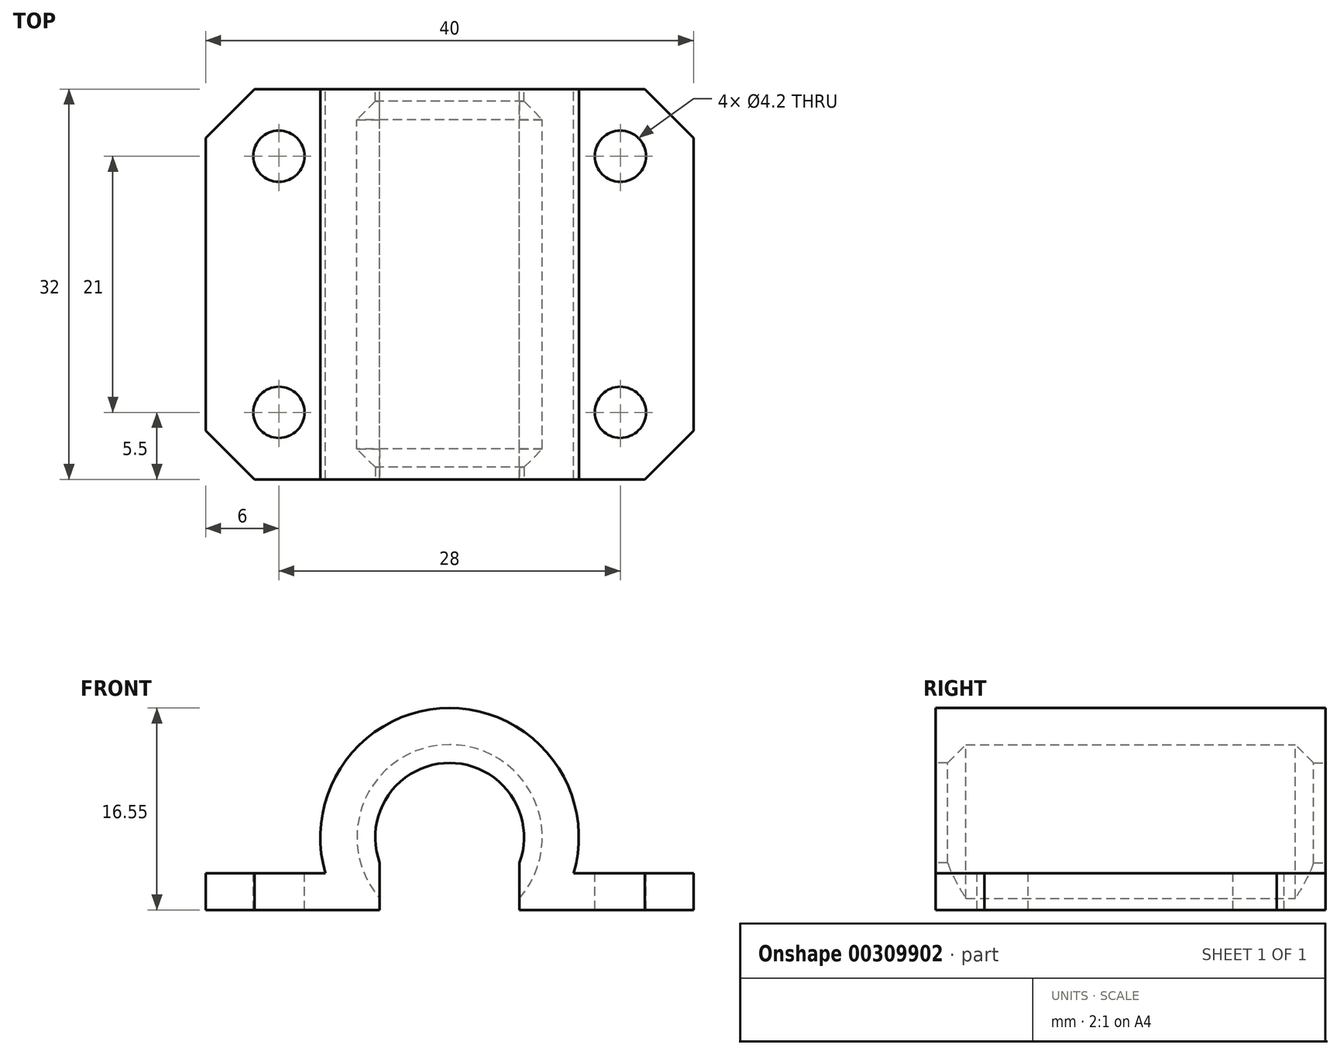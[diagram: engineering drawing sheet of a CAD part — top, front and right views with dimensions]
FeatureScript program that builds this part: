
annotation { "Feature Type Name" : "Feature", "Feature Type Description" : "" }
export const myFeature = defineFeature(function(context is Context, id is Id, definition is map)
    precondition{}
    {
        {
            var Q0;
            Q0=qCreatedBy(makeId("Front.planeOp"),FACE);
            var sketch = newSketch(context, id + "F0", { "sketchPlane" : qUnion([Q0])});
            skArc(sketch, "E0", {"start": v(0, 7.6) * mm, "mid": v(-6.92, 3.15) * mm, "end": v(-5.73, -5) * mm});
            skLineSegment(sketch, "E1", {"start": v(-4.73, -5.95) * mm, "end": v(-5.73, -5.95) * mm, "construction": true});
            skLineSegment(sketch, "E2", {"start": v(-20, -5.95) * mm, "end": v(-20, -2.95) * mm});
            skArc(sketch, "E3", {"start": v(0, 10.6) * mm, "mid": v(-8.47, 6.37) * mm, "end": v(-10.18, -2.95) * mm});
            skLineSegment(sketch, "E4", {"start": v(0, 10.6) * mm, "end": v(0, 7.6) * mm});
            skLineSegment(sketch, "E5", {"start": v(-20, -2.95) * mm, "end": v(-10.18, -2.95) * mm});
            skLineSegment(sketch, "E6", {"start": v(-5.73, -5.95) * mm, "end": v(-5.73, -5.95) * mm});
            skLineSegment(sketch, "E7", {"start": v(-5.73, -5.95) * mm, "end": v(-5.73, -5) * mm});
            skArc(sketch, "E8", {"start": v(-5.73, -5) * mm, "mid": v(-5.25, -5.5) * mm, "end": v(-4.73, -5.95) * mm, "construction": true});
            skLineSegment(sketch, "E9", {"start": v(-5.73, -5.95) * mm, "end": v(-20, -5.95) * mm});
            skLineSegment(sketch, "E10.MirrorCS", {"start": v(5.73, -5.95) * mm, "end": v(5.73, -5) * mm});
            skLineSegment(sketch, "E11.MirrorCS", {"start": v(4.73, -5.95) * mm, "end": v(5.73, -5.95) * mm, "construction": true});
            skArc(sketch, "E12.MirrorCS", {"start": v(5.73, -5) * mm, "mid": v(5.25, -5.5) * mm, "end": v(4.73, -5.95) * mm, "construction": true});
            skLineSegment(sketch, "E13.MirrorCS", {"start": v(5.73, -5.95) * mm, "end": v(5.73, -5.95) * mm});
            skArc(sketch, "E14.MirrorCS", {"start": v(0, 7.6) * mm, "mid": v(6.92, 3.15) * mm, "end": v(5.73, -5) * mm});
            skArc(sketch, "E15.MirrorCS", {"start": v(0, 10.6) * mm, "mid": v(8.47, 6.37) * mm, "end": v(10.18, -2.95) * mm});
            skLineSegment(sketch, "E16.MirrorCS", {"start": v(20, -2.95) * mm, "end": v(10.18, -2.95) * mm});
            skLineSegment(sketch, "E17.MirrorCS", {"start": v(20, -5.95) * mm, "end": v(20, -2.95) * mm});
            skLineSegment(sketch, "E18.MirrorCS", {"start": v(5.73, -5.95) * mm, "end": v(20, -5.95) * mm});
            skSolve(sketch);
        }
        {
            var Q0;
            Q0 = qSketchRegion(id + "F0", true);
            extrude(context, id + "F1", {"entities" : qUnion([Q0]), "depth" : 16 * mm});
        }
        {
            var Q0;
            Q0=makeQuery(id+"F1.opExtrude","SWEPT_FACE",FACE,{"disambiguationData":[OSD([sQuery(id+"F0.wireOp",EDGE,"E5")])]});
            var sketch = newSketch(context, id + "F2", { "sketchPlane" : qUnion([Q0])});
            skCircle(sketch, "E19", {"center": v(-14, -10.5) * mm, "radius": 2.1 * mm});
            skCircle(sketch, "E20", {"center": v(14, -10.5) * mm, "radius": 2.1 * mm});
            skSolve(sketch);
        }
        {
            var Q0;
            Q0 = qSketchRegion(id + "F2", true);
            extrude(context, id + "F3", {"entities" : qUnion([Q0]), "operationType" : NewBodyOperationType.REMOVE, "endBound" : BoundingType.UP_TO_NEXT, "oppositeDirection" : true, "depth" : 25 * mm});
        }
        {
            var Q0;
            Q0=makeQuery(id+"F1.opExtrude","CAP_EDGE",EDGE,{"disambiguationData":[OSD([sQuery(id+"F0.wireOp",EDGE,"E2")])],"isStart":false});
            var Q1;
            Q1=makeQuery(id+"F1.opExtrude","CAP_EDGE",EDGE,{"disambiguationData":[OSD([sQuery(id+"F0.wireOp",EDGE,"E17.MirrorCS")])],"isStart":false});
            chamfer(context, id + "F4", {"entities" : qUnion([Q0, Q1]), "width" : 4 * mm, "tangentPropagation" : true});
        }
        {
            var Q0;
            Q0=makeQuery(id+"F1.opExtrude","CAP_FACE",FACE,{"disambiguationData":[OSD([sQuery(id+"F0.wireOp",EDGE,"E0"),sQuery(id+"F0.wireOp",EDGE,"E2"),sQuery(id+"F0.wireOp",EDGE,"E3"),sQuery(id+"F0.wireOp",EDGE,"E5"),sQuery(id+"F0.wireOp",EDGE,"E7"),sQuery(id+"F0.wireOp",EDGE,"E9"),sQuery(id+"F0.wireOp",EDGE,"E10.MirrorCS"),sQuery(id+"F0.wireOp",EDGE,"E14.MirrorCS"),sQuery(id+"F0.wireOp",EDGE,"E15.MirrorCS"),sQuery(id+"F0.wireOp",EDGE,"E16.MirrorCS"),sQuery(id+"F0.wireOp",EDGE,"E17.MirrorCS"),sQuery(id+"F0.wireOp",EDGE,"E18.MirrorCS")])],"isStart":false});
            var sketch = newSketch(context, id + "F5", { "sketchPlane" : qUnion([Q0])});
            skArc(sketch, "E21", {"start": v(5.73, -5) * mm, "mid": v(0, 7.6) * mm, "end": v(-5.73, -5) * mm});
            skArc(sketch, "E22", {"start": v(5.73, -2.1) * mm, "mid": v(0, 6.1) * mm, "end": v(-5.73, -2.1) * mm});
            skLineSegment(sketch, "E23", {"start": v(-5.73, -5) * mm, "end": v(-5.73, -2.1) * mm});
            skLineSegment(sketch, "E24", {"start": v(5.73, -5) * mm, "end": v(5.73, -2.1) * mm});
            skSolve(sketch);
        }
        {
            var Q0;
            Q0 = qSketchRegion(id + "F5", true);
            extrude(context, id + "F6", {"entities" : qUnion([Q0]), "operationType" : NewBodyOperationType.ADD, "oppositeDirection" : true, "depth" : 2.5 * mm});
        }
        {
            var Q0;
            Q0=makeQuery(id+"F6.opExtrude","CAP_EDGE",EDGE,{"disambiguationData":[OSD([sQuery(id+"F5.wireOp",EDGE,"E22")])],"isStart":false});
            chamfer(context, id + "F7", {"entities" : qUnion([Q0]), "width" : 1.5 * mm, "tangentPropagation" : true});
        }
        {
            var Q0;
            Q0=makeQuery(id+"F1.opExtrude","SWEPT_BODY",BODY,{"disambiguationData":[OSD([sQuery(id+"F0.wireOp",EDGE,"E0"),sQuery(id+"F0.wireOp",EDGE,"E2"),sQuery(id+"F0.wireOp",EDGE,"E3"),sQuery(id+"F0.wireOp",EDGE,"E5"),sQuery(id+"F0.wireOp",EDGE,"E7"),sQuery(id+"F0.wireOp",EDGE,"E9"),sQuery(id+"F0.wireOp",EDGE,"E10.MirrorCS"),sQuery(id+"F0.wireOp",EDGE,"E14.MirrorCS"),sQuery(id+"F0.wireOp",EDGE,"E15.MirrorCS"),sQuery(id+"F0.wireOp",EDGE,"E16.MirrorCS"),sQuery(id+"F0.wireOp",EDGE,"E17.MirrorCS"),sQuery(id+"F0.wireOp",EDGE,"E18.MirrorCS")])]});
            var Q1;
            Q1=qCreatedBy(makeId("Front.planeOp"),FACE);
            mirror(context, id + "F8", {"operationType" : NewBodyOperationType.ADD, "entities" : qUnion([Q0]), "mirrorPlane" : qUnion([Q1])});
        }
    });
